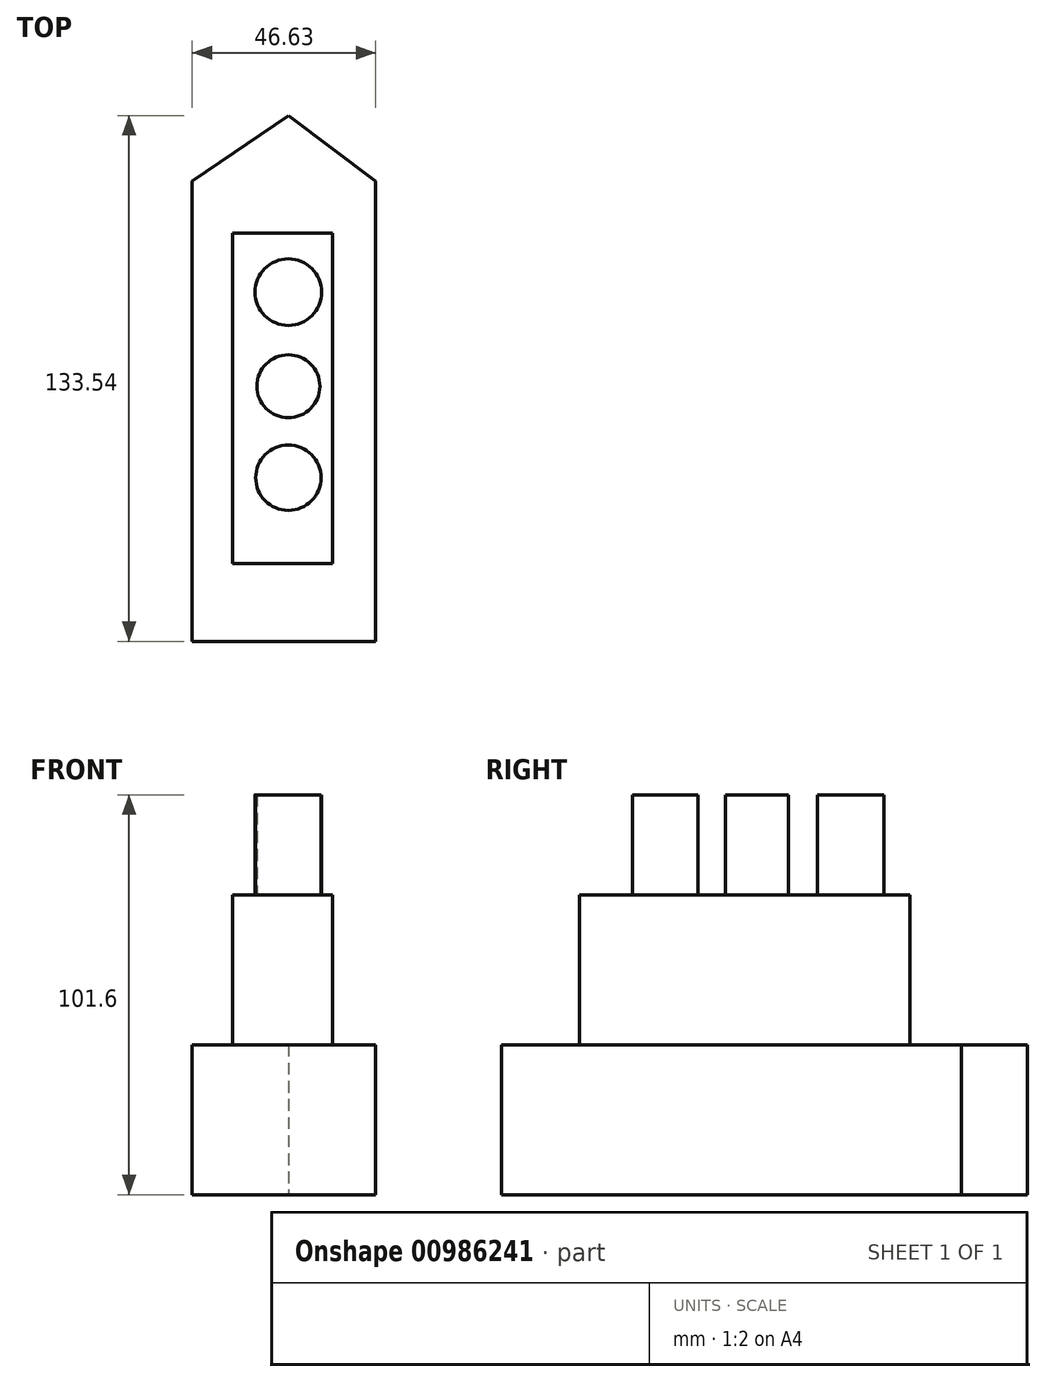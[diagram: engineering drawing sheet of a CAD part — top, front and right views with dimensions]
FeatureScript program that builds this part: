
annotation { "Feature Type Name" : "Feature", "Feature Type Description" : "" }
export const myFeature = defineFeature(function(context is Context, id is Id, definition is map)
    precondition{}
    {
        {
            var Q0;
            Q0=qCreatedBy(makeId("Top.planeOp"),FACE);
            var sketch = newSketch(context, id + "F0", { "sketchPlane" : qUnion([Q0])});
            skLineSegment(sketch, "E0", {"start": v(-24.44, 85.42) * mm, "end": v(-24.44, -31.43) * mm});
            skLineSegment(sketch, "E1", {"start": v(-24.44, 85.42) * mm, "end": v(0, 102.1) * mm});
            skLineSegment(sketch, "E2", {"start": v(0, 102.1) * mm, "end": v(22.19, 85.42) * mm});
            skLineSegment(sketch, "E3", {"start": v(22.19, 85.42) * mm, "end": v(22.19, -31.43) * mm});
            skLineSegment(sketch, "E4", {"start": v(22.19, -31.43) * mm, "end": v(-24.44, -31.43) * mm});
            skSolve(sketch);
        }
        {
            var Q0;
            Q0 = qSketchRegion(id + "F0", true);
            extrude(context, id + "F1", {"entities" : qUnion([Q0]), "depth" : 38.1 * mm, "offsetDistance" : 25.4 * mm});
        }
        {
            var Q0;
            Q0=qCreatedBy(makeId("Top.planeOp"),FACE);
            var sketch = newSketch(context, id + "F2", { "sketchPlane" : qUnion([Q0])});
            skLineSegment(sketch, "E5.bottom", {"start": v(-14.22, 72.24) * mm, "end": v(11.18, 72.24) * mm});
            skLineSegment(sketch, "E5.top", {"start": v(-14.22, -11.64) * mm, "end": v(11.18, -11.64) * mm});
            skLineSegment(sketch, "E5.left", {"start": v(-14.22, 72.24) * mm, "end": v(-14.22, -11.64) * mm});
            skLineSegment(sketch, "E5.right", {"start": v(11.18, 72.24) * mm, "end": v(11.18, -11.64) * mm});
            skSolve(sketch);
        }
        {
            var Q0;
            Q0 = qSketchRegion(id + "F2", true);
            extrude(context, id + "F3", {"entities" : qUnion([Q0]), "operationType" : NewBodyOperationType.ADD, "depth" : 76.2 * mm, "offsetDistance" : 25.4 * mm});
        }
        {
            var Q0;
            Q0=qCreatedBy(makeId("Top.planeOp"),FACE);
            var sketch = newSketch(context, id + "F4", { "sketchPlane" : qUnion([Q0])});
            skCircle(sketch, "E6", {"center": v(0, 57.28) * mm, "radius": 8.47 * mm});
            skCircle(sketch, "E7", {"center": v(0, 33.37) * mm, "radius": 8 * mm});
            skCircle(sketch, "E8", {"center": v(0, 10.14) * mm, "radius": 8.3 * mm});
            skSolve(sketch);
        }
        {
            var Q0;
            Q0 = qSketchRegion(id + "F4", true);
            extrude(context, id + "F5", {"entities" : qUnion([Q0]), "operationType" : NewBodyOperationType.ADD, "depth" : 101.6 * mm, "offsetDistance" : 25.4 * mm});
        }
        {
            var Q0;
            Q0=makeQuery(id+"F3.opExtrude","SWEPT_FACE",FACE,{"disambiguationData":[OSD([sQuery(id+"F2.wireOp",EDGE,"E5.right")])]});
            var sketch = newSketch(context, id + "F6", { "sketchPlane" : qUnion([Q0])});
            skText(sketch, "E9", { "text": "F&O\n", "fontName": "OpenSans-Regular.ttf"});
            skPoint(sketch, "E9.firstSnap0", {"position": v(72.24, 57.15) * mm});
            const initialGuessF6  = {"E9": [0, 0.0381, 1, 0, 0.0225]};
            skSetInitialGuess(sketch, initialGuessF6);
            skSolve(sketch);
        }
        {
            var Q0;
            Q0 = qConstructionFilter(qBodyType(qCreatedBy(id + "F6" ,EDGE), BodyType.WIRE), ConstructionObject.NO);
            extrude(context, id + "F7", {"bodyType" : ToolBodyType.SURFACE, "surfaceEntities" : qUnion([Q0]), "oppositeDirection" : true, "depth" : 17.27 * mm, "offsetDistance" : 25.4 * mm});
        }
    });
